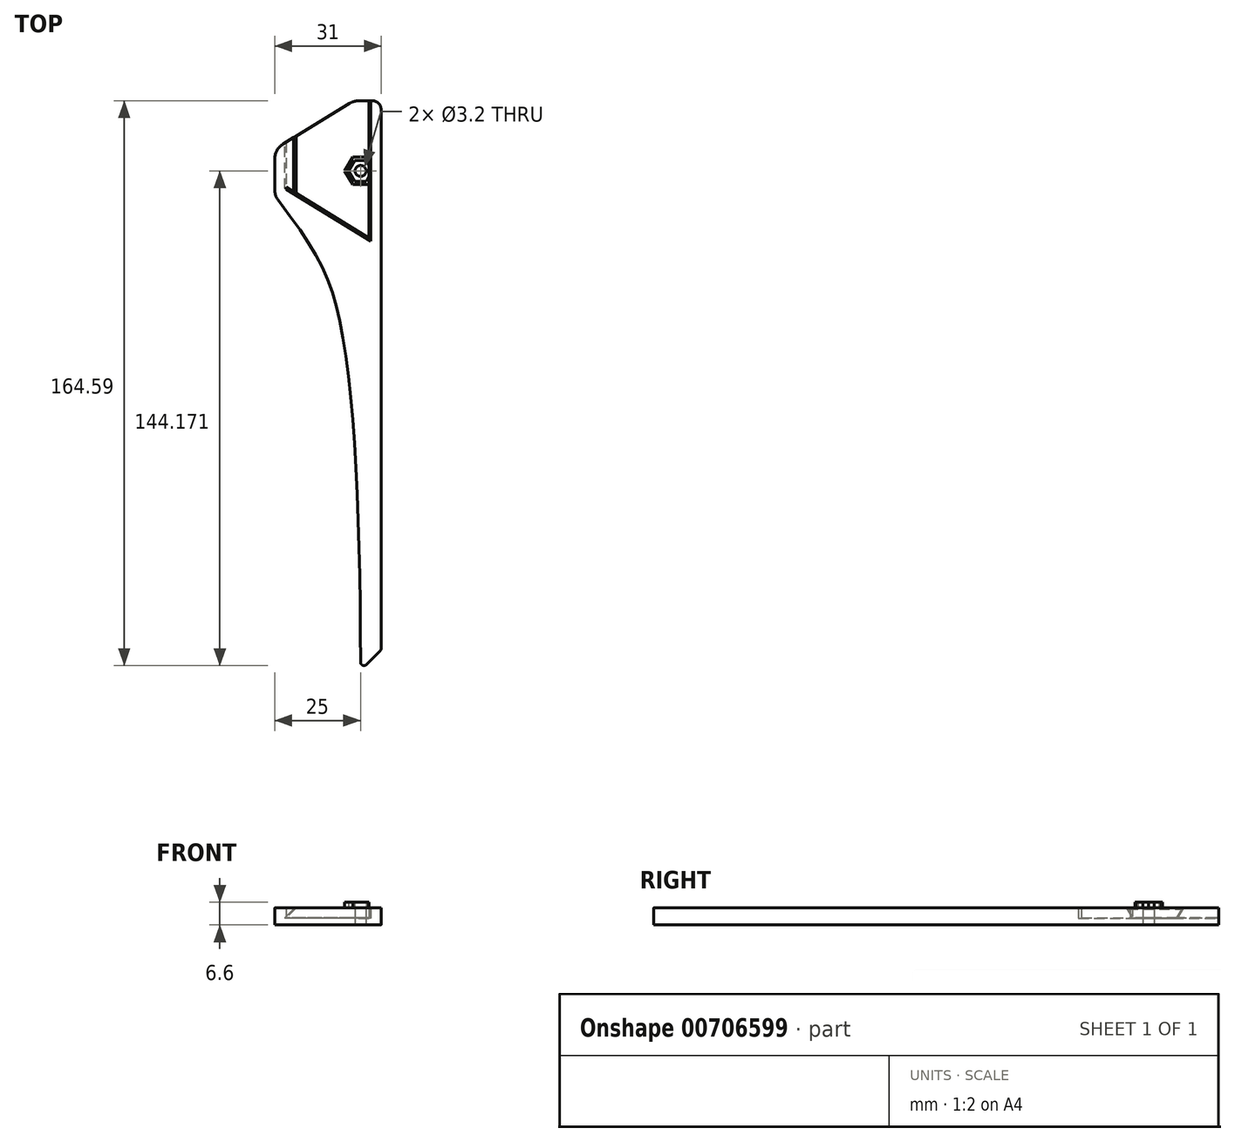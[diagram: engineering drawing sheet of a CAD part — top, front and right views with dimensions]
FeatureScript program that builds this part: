
annotation { "Feature Type Name" : "Feature", "Feature Type Description" : "" }
export const myFeature = defineFeature(function(context is Context, id is Id, definition is map)
    precondition{}
    {
        {
            var Q0;
            Q0=qCreatedBy(makeId("Top.planeOp"),FACE);
            var sketch = newSketch(context, id + "F0", { "sketchPlane" : qUnion([Q0])});
            skLineSegment(sketch, "E0", {"start": v(0, 0) * mm, "end": v(0, 39) * mm, "construction": true});
            skLineSegment(sketch, "E1", {"start": v(0, 39) * mm, "end": v(18, 28) * mm, "construction": true});
            skLineSegment(sketch, "E2", {"start": v(18, 28) * mm, "end": v(18, 24.39) * mm, "construction": true});
            skLineSegment(sketch, "E3", {"start": v(18, -11) * mm, "end": v(0, 0) * mm, "construction": true});
            skLineSegment(sketch, "E4.0", {"start": v(-1, -0.56) * mm, "end": v(-1, 39) * mm});
            skLineSegment(sketch, "E4.1", {"start": v(19, -12.78) * mm, "end": v(-1, -0.56) * mm});
            skLineSegment(sketch, "E4.2", {"start": v(19, 28) * mm, "end": v(19, -12.78) * mm, "construction": true});
            skLineSegment(sketch, "E5", {"start": v(19, 25) * mm, "end": v(-4, 10.94) * mm});
            skLineSegment(sketch, "E6", {"start": v(18, 24.39) * mm, "end": v(18, -11) * mm, "construction": true});
            skLineSegment(sketch, "E7", {"start": v(18, 26.2) * mm, "end": v(0, 26.2) * mm, "construction": true});
            skLineSegment(sketch, "E8", {"start": v(10.43, 32.62) * mm, "end": v(10.43, 26.2) * mm, "construction": true});
            skLineSegment(sketch, "E9", {"start": v(10.43, 26.2) * mm, "end": v(10.43, 19.77) * mm, "construction": true});
            skLineSegment(sketch, "E10", {"start": v(-4, 10.94) * mm, "end": v(-4, -2.6) * mm});
            skLineSegment(sketch, "E11", {"start": v(19, 25) * mm, "end": v(27, 25) * mm});
            skLineSegment(sketch, "E12", {"start": v(27, 25) * mm, "end": v(27, -135) * mm});
            skLineSegment(sketch, "E13", {"start": v(27, -135) * mm, "end": v(21, -141) * mm});
            skLineSegment(sketch, "E14", {"start": v(19, -12.78) * mm, "end": v(24, -15.84) * mm});
            skLineSegment(sketch, "E15", {"start": v(24, -15.84) * mm, "end": v(24, 25) * mm});
            skCircle(sketch, "E16", {"center": v(21, 4.58) * mm, "radius": 1.6 * mm});
            skPoint(sketch, "E16.centerSnap0", {"position": v(24, 4.58) * mm});
            skLineSegment(sketch, "E17", {"start": v(1.5, -2.09) * mm, "end": v(1.5, 14.3) * mm});
            skFitSpline(sketch, "E18", {"points": [v(21, -141) * mm, v(14.75, -38.2) * mm, v(-4, -2.6) * mm], "startDerivative": vector(0, 202.15) * mm, "endDerivative": vector(-88.82, 116.9) * mm});
            skSolve(sketch);
        }
        {
            var Q0;
            {var subQ5=sQuery(id+"F0.wireOp",EDGE,"E4.1");Q0=makeQuery(id+"F0.imprint","IMPRINT",FACE,{"disambiguationData":[TD([[makeQuery(id+"F0.imprint","IMPRINT",EDGE,{"derivedFrom":subQ5}),-1.0]])]});}
            var Q1;
            {var subQ0=sQuery(id+"F0.wireOp",EDGE,"E14");Q1=makeQuery(id+"F0.imprint","IMPRINT",FACE,{"disambiguationData":[TD([[makeQuery(id+"F0.imprint","IMPRINT",EDGE,{"derivedFrom":subQ0}),1.0]])]});}
            extrude(context, id + "F1", {"entities" : qUnion([Q0, Q1]), "depth" : 2 * mm, "offsetDistance" : 25 * mm});
        }
        {
            var Q0;
            {var subQ4=sQuery(id+"F0.wireOp",EDGE,"E4.1");Q0=makeQuery(id+"F0.imprint","IMPRINT",FACE,{"disambiguationData":[TD([[makeQuery(id+"F0.imprint","IMPRINT",EDGE,{"derivedFrom":subQ4}),1.0]])]});}
            extrude(context, id + "F2", {"entities" : qUnion([Q0]), "operationType" : NewBodyOperationType.ADD, "depth" : 5 * mm, "offsetDistance" : 25 * mm});
        }
        {
            var Q0;
            {var subQ5=sQuery(id+"F0.wireOp",EDGE,"E17");Q0=makeQuery(id+"F0.imprint","IMPRINT",FACE,{"disambiguationData":[TD([[makeQuery(id+"F0.imprint","IMPRINT",EDGE,{"derivedFrom":subQ5}),1.0]])]});}
            var Q1;
            Q1=makeQuery(id+"F2.opExtrude","CAP_FACE",FACE,{"disambiguationData":[OSD([sQuery(id+"F0.wireOp",EDGE,"E4.0"),sQuery(id+"F0.wireOp",EDGE,"E4.1"),sQuery(id+"F0.wireOp",EDGE,"E5"),sQuery(id+"F0.wireOp",EDGE,"E10"),sQuery(id+"F0.wireOp",EDGE,"E11"),sQuery(id+"F0.wireOp",EDGE,"E12"),sQuery(id+"F0.wireOp",EDGE,"E13"),sQuery(id+"F0.wireOp",EDGE,"e687ead8-f1bc-4273-8f4c-0fbf44d02dc6"),sQuery(id+"F0.wireOp",EDGE,"E14"),sQuery(id+"F0.wireOp",EDGE,"E15")])],"isStart":false});
            extrude(context, id + "F3", {"entities" : qUnion([Q0]), "operationType" : NewBodyOperationType.ADD, "endBound" : BoundingType.UP_TO_SURFACE, "depth" : 2.2 * mm, "endBoundEntityFace" : qUnion([Q1]), "offsetDistance" : 25 * mm, "hasSecondDirection" : true, "secondDirectionOppositeDirection" : false, "secondDirectionDepth" : 2.1 * mm});
        }
        {
            var Q0;
            Q0=makeQuery(id+"F3.opExtrude","CAP_EDGE",EDGE,{"disambiguationData":[OSD([sQuery(id+"F0.wireOp",EDGE,"E17")])],"isStart":true});
            chamfer(context, id + "F4", {"entities" : qUnion([Q0]), "width" : 2.5 * mm, "tangentPropagation" : true});
        }
        {
            var Q0;
            Q0=makeQuery(id+"F2.opExtrude","SWEPT_EDGE",EDGE,{"disambiguationData":[OSD([sQuery(id+"F0.wireOp",EDGE,"E10"),sQuery(id+"F0.wireOp",EDGE,"e687ead8-f1bc-4273-8f4c-0fbf44d02dc6")])]});
            var Q1;
            Q1=makeQuery(id+"F2.opExtrude","SWEPT_EDGE",EDGE,{"disambiguationData":[OSD([sQuery(id+"F0.wireOp",EDGE,"E5"),sQuery(id+"F0.wireOp",EDGE,"E10")])]});
            var Q2;
            Q2=makeQuery(id+"F1.opExtrude","SWEPT_EDGE",EDGE,{"disambiguationData":[OSD([sQuery(id+"F0.wireOp",EDGE,"E5"),sQuery(id+"F0.wireOp",EDGE,"E11")])]});
            fillet(context, id + "F5", {"entities" : qUnion([Q0, Q1, Q2]), "radius" : 5 * mm, "tangentPropagation" : true, "allowEdgeOverflow" : false});
        }
        {
            var Q0;
            Q0=makeQuery(id+"F2.opExtrude","SWEPT_EDGE",EDGE,{"disambiguationData":[OSD([sQuery(id+"F0.wireOp",EDGE,"E11"),sQuery(id+"F0.wireOp",EDGE,"E12")])]});
            fillet(context, id + "F6", {"entities" : qUnion([Q0]), "radius" : 2.5 * mm, "tangentPropagation" : true, "allowEdgeOverflow" : false});
        }
        {
            var Q0;
            Q0=makeQuery(id+"F2.opExtrude","SWEPT_EDGE",EDGE,{"disambiguationData":[OSD([sQuery(id+"F0.wireOp",EDGE,"E12"),sQuery(id+"F0.wireOp",EDGE,"E13")])]});
            var Q1;
            Q1=makeQuery(id+"F2.opExtrude","SWEPT_EDGE",EDGE,{"disambiguationData":[OSD([sQuery(id+"F0.wireOp",EDGE,"E13"),sQuery(id+"F0.wireOp",EDGE,"e687ead8-f1bc-4273-8f4c-0fbf44d02dc6")])]});
            fillet(context, id + "F7", {"entities" : qUnion([Q0, Q1]), "radius" : 1 * mm, "tangentPropagation" : true, "allowEdgeOverflow" : false});
        }
        {
            var Q0;
            {var subQ5=sQuery(id+"F0.wireOp",EDGE,"E17");Q0=makeQuery(id+"F0.imprint","IMPRINT",FACE,{"disambiguationData":[TD([[makeQuery(id+"F0.imprint","IMPRINT",EDGE,{"derivedFrom":subQ5}),1.0]])]});}
            var Q1;
            {var subQ0=sQuery(id+"F0.wireOp",EDGE,"E14");Q1=makeQuery(id+"F0.imprint","IMPRINT",FACE,{"disambiguationData":[TD([[makeQuery(id+"F0.imprint","IMPRINT",EDGE,{"derivedFrom":subQ0}),1.0]])]});}
            extrude(context, id + "F8", {"entities" : qUnion([Q0, Q1]), "depth" : 5 * mm, "offsetDistance" : 25 * mm, "hasSecondDirection" : true, "secondDirectionOppositeDirection" : false, "secondDirectionDepth" : 2.1 * mm});
        }
        {
            var Q0;
            Q0=makeQuery(id+"F8.opExtrude","CAP_EDGE",EDGE,{"disambiguationData":[OSD([sQuery(id+"F0.wireOp",EDGE,"E4.0")])],"isStart":false});
            chamfer(context, id + "F9", {"entities" : qUnion([Q0]), "width" : 3.2 * mm, "tangentPropagation" : true});
        }
        {
            var Q0;
            Q0=makeQuery(id+"F8.opExtrude","CAP_FACE",FACE,{"disambiguationData":[OSD([sQuery(id+"F0.wireOp",EDGE,"E4.0"),sQuery(id+"F0.wireOp",EDGE,"E4.1"),sQuery(id+"F0.wireOp",EDGE,"E5"),sQuery(id+"F0.wireOp",EDGE,"E11"),sQuery(id+"F0.wireOp",EDGE,"E14"),sQuery(id+"F0.wireOp",EDGE,"E15"),sQuery(id+"F0.wireOp",EDGE,"E16")])],"isStart":true});
            var sketch = newSketch(context, id + "F10", { "sketchPlane" : qUnion([Q0])});
            skLineSegment(sketch, "E19.0", {"start": v(24, 15.84) * mm, "end": v(24, -25) * mm});
            skLineSegment(sketch, "E20.0", {"start": v(24, 15.84) * mm, "end": v(-0.7, 0.74) * mm});
            skLineSegment(sketch, "E21.0", {"start": v(23.5, 14.95) * mm, "end": v(-0.44, 0.32) * mm});
            skLineSegment(sketch, "E21.1", {"start": v(23.5, 14.95) * mm, "end": v(23.5, -25) * mm});
            skLineSegment(sketch, "E22", {"start": v(-0.44, 0.32) * mm, "end": v(-0.7, 0.16) * mm});
            skLineSegment(sketch, "E23", {"start": v(-0.7, 0.16) * mm, "end": v(-0.7, 0.74) * mm});
            skLineSegment(sketch, "E24", {"start": v(24, -25) * mm, "end": v(23.5, -25) * mm});
            skCircle(sketch, "E25.0", {"center": v(21, -4.58) * mm, "radius": 1.6 * mm});
            skCircle(sketch, "E26.cCircle", {"center": v(21, -4.58) * mm, "radius": 3 * mm, "construction": true});
            skLineSegment(sketch, "E26.0", {"start": v(22.73, -7.58) * mm, "end": v(19.27, -7.58) * mm});
            skLineSegment(sketch, "E26.1", {"start": v(19.27, -7.58) * mm, "end": v(17.54, -4.58) * mm});
            skLineSegment(sketch, "E26.2", {"start": v(17.54, -4.58) * mm, "end": v(19.27, -1.58) * mm});
            skLineSegment(sketch, "E26.3", {"start": v(19.27, -1.58) * mm, "end": v(22.73, -1.58) * mm});
            skLineSegment(sketch, "E26.4", {"start": v(22.73, -1.58) * mm, "end": v(24.46, -4.58) * mm});
            skLineSegment(sketch, "E26.5", {"start": v(24.46, -4.58) * mm, "end": v(22.73, -7.58) * mm});
            skPoint(sketch, "E26.0.midPoint", {"position": v(21, -7.58) * mm});
            skCircle(sketch, "E27.cCircle", {"center": v(21, -4.58) * mm, "radius": 4 * mm, "construction": true});
            skLineSegment(sketch, "E27.0", {"start": v(23.3, -8.58) * mm, "end": v(18.7, -8.58) * mm});
            skLineSegment(sketch, "E27.1", {"start": v(18.7, -8.58) * mm, "end": v(16.38, -4.58) * mm});
            skLineSegment(sketch, "E27.2", {"start": v(16.38, -4.58) * mm, "end": v(18.7, -0.58) * mm});
            skLineSegment(sketch, "E27.3", {"start": v(18.7, -0.58) * mm, "end": v(23.3, -0.58) * mm});
            skLineSegment(sketch, "E27.4", {"start": v(23.3, -0.58) * mm, "end": v(25.62, -4.58) * mm});
            skLineSegment(sketch, "E27.5", {"start": v(25.62, -4.58) * mm, "end": v(23.3, -8.58) * mm});
            skPoint(sketch, "E27.0.midPoint", {"position": v(21, -8.58) * mm});
            skSolve(sketch);
        }
        {
            var Q0;
            {var subQ4=sQuery(id+"F10.wireOp",EDGE,"E20.0");Q0=makeQuery(id+"F10.imprint","IMPRINT",FACE,{"disambiguationData":[TD([[makeQuery(id+"F10.imprint","IMPRINT",EDGE,{"derivedFrom":subQ4}),1.0]])]});}
            var Q1;
            {var subQ0=sQuery(id+"F10.wireOp",EDGE,"E24");Q1=makeQuery(id+"F10.imprint","IMPRINT",FACE,{"disambiguationData":[TD([[makeQuery(id+"F10.imprint","IMPRINT",EDGE,{"derivedFrom":subQ0}),1.0]])]});}
            var Q2;
            {var subQ0=sQuery(id+"F10.wireOp",EDGE,"E27.4");var subQ1=sQuery(id+"F10.wireOp",EDGE,"E19.0");var subQ2=makeQuery(id+"F10.imprint","INTERSECT",VERTEX,{"derivedFrom":[subQ1,subQ0]});Q2=makeQuery(id+"F10.imprint","IMPRINT",FACE,{"disambiguationData":[TD([[makeQuery(id+"F10.imprint","IMPRINT",EDGE,{"disambiguationData":[TD([[subQ2,-1.0]])],"derivedFrom":subQ1}),-1.0]])]});}
            var Q3;
            {var subQ0=sQuery(id+"F10.wireOp",EDGE,"E27.5");var subQ1=sQuery(id+"F10.wireOp",EDGE,"E19.0");var subQ2=makeQuery(id+"F10.imprint","INTERSECT",VERTEX,{"derivedFrom":[subQ1,subQ0]});Q3=makeQuery(id+"F10.imprint","IMPRINT",FACE,{"disambiguationData":[TD([[makeQuery(id+"F10.imprint","IMPRINT",EDGE,{"disambiguationData":[TD([[subQ2,1.0]])],"derivedFrom":subQ1}),-1.0]])]});}
            var Q4;
            {var subQ0=sQuery(id+"F10.wireOp",EDGE,"E26.4");var subQ1=sQuery(id+"F10.wireOp",EDGE,"E19.0");var subQ2=makeQuery(id+"F10.imprint","INTERSECT",VERTEX,{"derivedFrom":[subQ1,subQ0]});Q4=makeQuery(id+"F10.imprint","IMPRINT",FACE,{"disambiguationData":[TD([[makeQuery(id+"F10.imprint","IMPRINT",EDGE,{"disambiguationData":[TD([[subQ2,-1.0]])],"derivedFrom":subQ1}),-1.0]])]});}
            var Q5;
            Q5=makeQuery(id+"F8.opExtrude","CAP_FACE",FACE,{"disambiguationData":[OSD([sQuery(id+"F0.wireOp",EDGE,"E4.0"),sQuery(id+"F0.wireOp",EDGE,"E4.1"),sQuery(id+"F0.wireOp",EDGE,"E5"),sQuery(id+"F0.wireOp",EDGE,"E11"),sQuery(id+"F0.wireOp",EDGE,"E14"),sQuery(id+"F0.wireOp",EDGE,"E15"),sQuery(id+"F0.wireOp",EDGE,"E16")])],"isStart":false});
            extrude(context, id + "F11", {"entities" : qUnion([Q0, Q1, Q2, Q3, Q4]), "operationType" : NewBodyOperationType.REMOVE, "endBound" : BoundingType.UP_TO_SURFACE, "oppositeDirection" : true, "depth" : 25 * mm, "endBoundEntityFace" : qUnion([Q5]), "offsetDistance" : 25 * mm});
        }
        {
            var Q0;
            {var subQ2=sQuery(id+"F10.wireOp",EDGE,"E26.0");Q0=makeQuery(id+"F10.imprint","IMPRINT",FACE,{"disambiguationData":[TD([[makeQuery(id+"F10.imprint","IMPRINT",EDGE,{"derivedFrom":subQ2}),1.0]])]});}
            var Q1;
            Q1=makeQuery(id+"F8.opExtrude","CAP_FACE",FACE,{"disambiguationData":[OSD([sQuery(id+"F0.wireOp",EDGE,"E4.0"),sQuery(id+"F0.wireOp",EDGE,"E4.1"),sQuery(id+"F0.wireOp",EDGE,"E5"),sQuery(id+"F0.wireOp",EDGE,"E11"),sQuery(id+"F0.wireOp",EDGE,"E14"),sQuery(id+"F0.wireOp",EDGE,"E15"),sQuery(id+"F0.wireOp",EDGE,"E16")])],"isStart":false});
            extrude(context, id + "F12", {"entities" : qUnion([Q0]), "operationType" : NewBodyOperationType.ADD, "oppositeDirection" : true, "depth" : 4.5 * mm, "offsetDistance" : 25 * mm});
        }
        {
            var Q0;
            Q0=makeQuery(id+"F8.opExtrude","SWEPT_EDGE",EDGE,{"disambiguationData":[OSD([sQuery(id+"F0.wireOp",EDGE,"E5"),sQuery(id+"F0.wireOp",EDGE,"E11")])]});
            fillet(context, id + "F13", {"entities" : qUnion([Q0]), "radius" : 5 * mm, "tangentPropagation" : true, "allowEdgeOverflow" : false});
        }
    });
